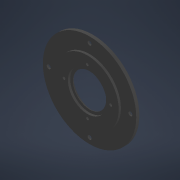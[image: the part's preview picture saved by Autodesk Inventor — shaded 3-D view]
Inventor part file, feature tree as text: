
AUTODESK INVENTOR PART (.ipt)
format: ipt  version: 2022 (Build 260153070, 153G)  size: 172,544 bytes
history: native  units: mm
features: sketch x5, hole x3, extrude x2, pattern_circular x2, other x1, chamfer x1
ambient origin geometry x8: Origin, YZ Plane, XZ Plane, XY Plane, X Axis, Y Axis, Z Axis, Center Point
bodies: Body1 (feature_tree)
feature tree (14):
  other  "Твердое тело1"
  extrude  "Выдавливание1"  Depth=104.0mm
  sketch  "Эскиз2"
  extrude  "Выдавливание2"  Depth=37.0mm
  chamfer  "Фаска1"  Distance=3.5mm
  hole  "Отверстие1"  [1 undecoded]
  hole  "Отверстие2"  [1 undecoded]
  pattern_circular  "Круговой массив1"  Angle=45.0deg  [1 undecoded]
  hole  "Отверстие3"  [1 undecoded]
  pattern_circular  "Круговой массив2"  Count=4 Angle=360.0deg
  sketch  "Эскиз1"
  sketch  "Эскиз3"
  sketch  "Эскиз4"
  sketch  "Эскиз5"
note: 4 required parameter values undecoded (feature->parameter linkage not recoverable at this tier; creation-order binding heuristic only, values carry confidence <= 0.55)
